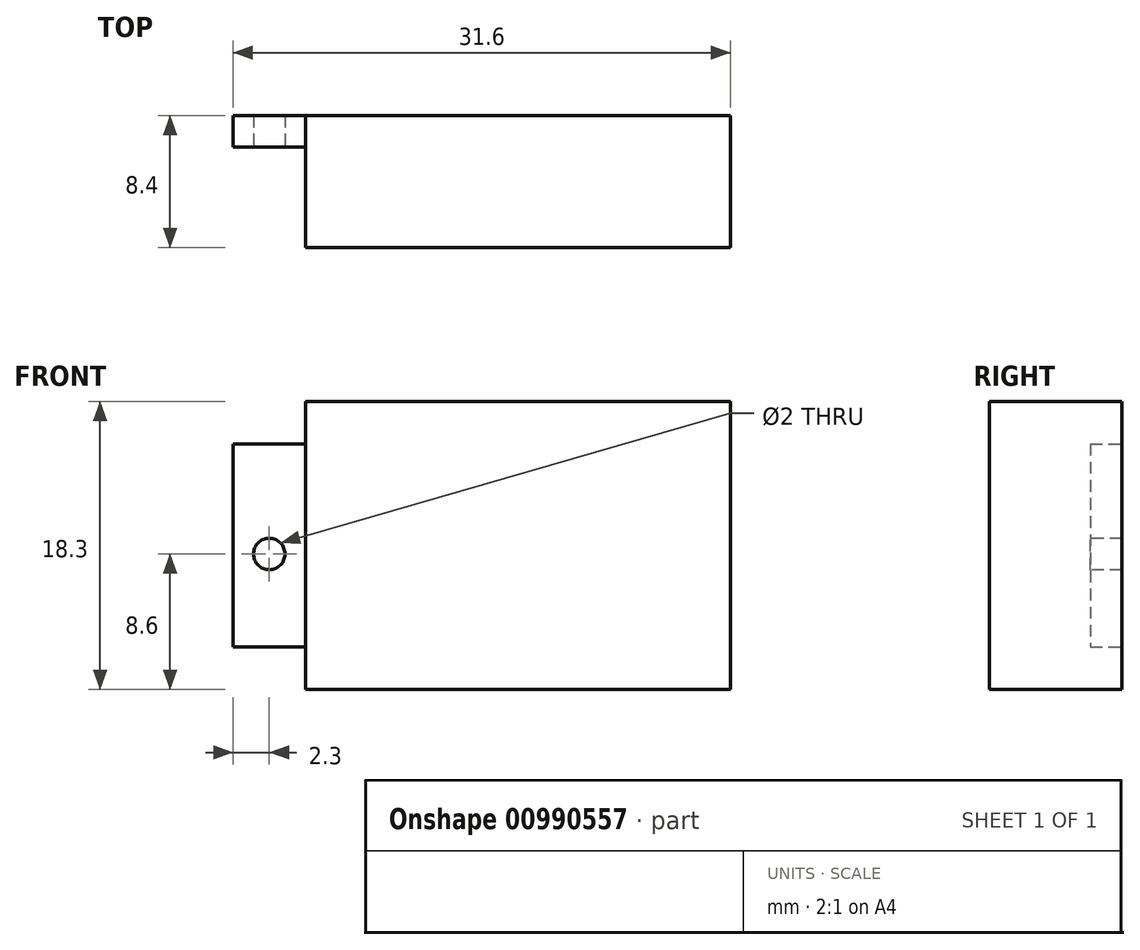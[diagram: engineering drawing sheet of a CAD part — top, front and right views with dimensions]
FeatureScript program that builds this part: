
annotation { "Feature Type Name" : "Feature", "Feature Type Description" : "" }
export const myFeature = defineFeature(function(context is Context, id is Id, definition is map)
    precondition{}
    {
        {
            var Q0;
            Q0=qCreatedBy(makeId("Front.planeOp"),FACE);
            var sketch = newSketch(context, id + "F0", { "sketchPlane" : qUnion([Q0])});
            skLineSegment(sketch, "E0.bottom", {"start": v(-13.5, -9.15) * mm, "end": v(13.5, -9.15) * mm});
            skLineSegment(sketch, "E0.top", {"start": v(-13.5, 9.15) * mm, "end": v(13.5, 9.15) * mm});
            skLineSegment(sketch, "E0.left", {"start": v(-13.5, -9.15) * mm, "end": v(-13.5, 9.15) * mm});
            skLineSegment(sketch, "E0.right", {"start": v(13.5, -9.15) * mm, "end": v(13.5, 9.15) * mm});
            skPoint(sketch, "E0.middle", {"position": v(0, 0) * mm});
            skSolve(sketch);
        }
        {
            var Q0;
            Q0=makeQuery(id+"F0.imprint","IMPRINT",FACE,{"disambiguationData":[TD([[makeQuery(id+"F0.imprint","IMPRINT",EDGE,{"derivedFrom":sQuery(id+"F0.wireOp",EDGE,"E0.bottom")}),1.0]])]});
            extrude(context, id + "F1", {"entities" : qUnion([Q0]), "depth" : 8.4 * mm, "offsetDistance" : 25 * mm});
        }
        {
            var Q0;
            Q0=makeQuery(id+"F1.opExtrude","CAP_FACE",FACE,{"disambiguationData":[OSD([sQuery(id+"F0.wireOp",EDGE,"E0.bottom"),sQuery(id+"F0.wireOp",EDGE,"E0.top"),sQuery(id+"F0.wireOp",EDGE,"E0.left"),sQuery(id+"F0.wireOp",EDGE,"E0.right")])],"isStart":true});
            var sketch = newSketch(context, id + "F2", { "sketchPlane" : qUnion([Q0])});
            skLineSegment(sketch, "E1.bottom", {"start": v(18.1, 6.45) * mm, "end": v(13.5, 6.45) * mm});
            skLineSegment(sketch, "E1.top", {"start": v(18.1, -6.45) * mm, "end": v(13.5, -6.45) * mm});
            skLineSegment(sketch, "E1.left", {"start": v(18.1, 6.45) * mm, "end": v(18.1, -6.45) * mm});
            skLineSegment(sketch, "E1.right", {"start": v(13.5, 6.45) * mm, "end": v(13.5, -6.45) * mm});
            skPoint(sketch, "E1.middle", {"position": v(15.8, 0) * mm});
            skPoint(sketch, "E1.middle.positionSnap0", {"position": v(13.5, 0) * mm});
            skPoint(sketch, "E1.centerSnap0", {"position": v(13.5, 0) * mm});
            skSolve(sketch);
        }
        {
            var Q0;
            Q0=makeQuery(id+"F2.imprint","IMPRINT",FACE,{"disambiguationData":[TD([[makeQuery(id+"F2.imprint","IMPRINT",EDGE,{"derivedFrom":sQuery(id+"F2.wireOp",EDGE,"E1.bottom")}),1.0]])]});
            extrude(context, id + "F3", {"entities" : qUnion([Q0]), "depth" : -2 * mm, "offsetDistance" : 25 * mm});
        }
        {
            var Q0;
            Q0=makeQuery(id+"F3.opExtrude","CAP_FACE",FACE,{"disambiguationData":[OSD([sQuery(id+"F2.wireOp",EDGE,"E1.bottom"),sQuery(id+"F2.wireOp",EDGE,"E1.top"),sQuery(id+"F2.wireOp",EDGE,"E1.left"),sQuery(id+"F2.wireOp",EDGE,"E1.right")])],"isStart":false});
            var sketch = newSketch(context, id + "F4", { "sketchPlane" : qUnion([Q0])});
            skCircle(sketch, "E2", {"center": v(-15.8, -0.55) * mm, "radius": 1 * mm});
            skSolve(sketch);
        }
        {
            var Q0;
            Q0=sQuery(id+"F4.wireOp",VERTEX,"E2.center");
            var Q1;
            Q1=makeQuery(id+"F3.opExtrude","SWEPT_BODY",BODY,{"disambiguationData":[OSD([sQuery(id+"F2.wireOp",EDGE,"E1.bottom"),sQuery(id+"F2.wireOp",EDGE,"E1.top"),sQuery(id+"F2.wireOp",EDGE,"E1.left"),sQuery(id+"F2.wireOp",EDGE,"E1.right")])]});
            hole(context, id + "F5", {"style" : HoleStyle.SIMPLE, "endStyle" : HoleEndStyle.THROUGH, "holeDiameter" : 2 * mm, "majorDiameter" : 5 * mm, "isTappedThrough" : true, "tappedDepth" : 12 * mm, "tapClearance" : 3, "locations" : qUnion([Q0]), "scope" : qUnion([Q1])});
        }
    });
